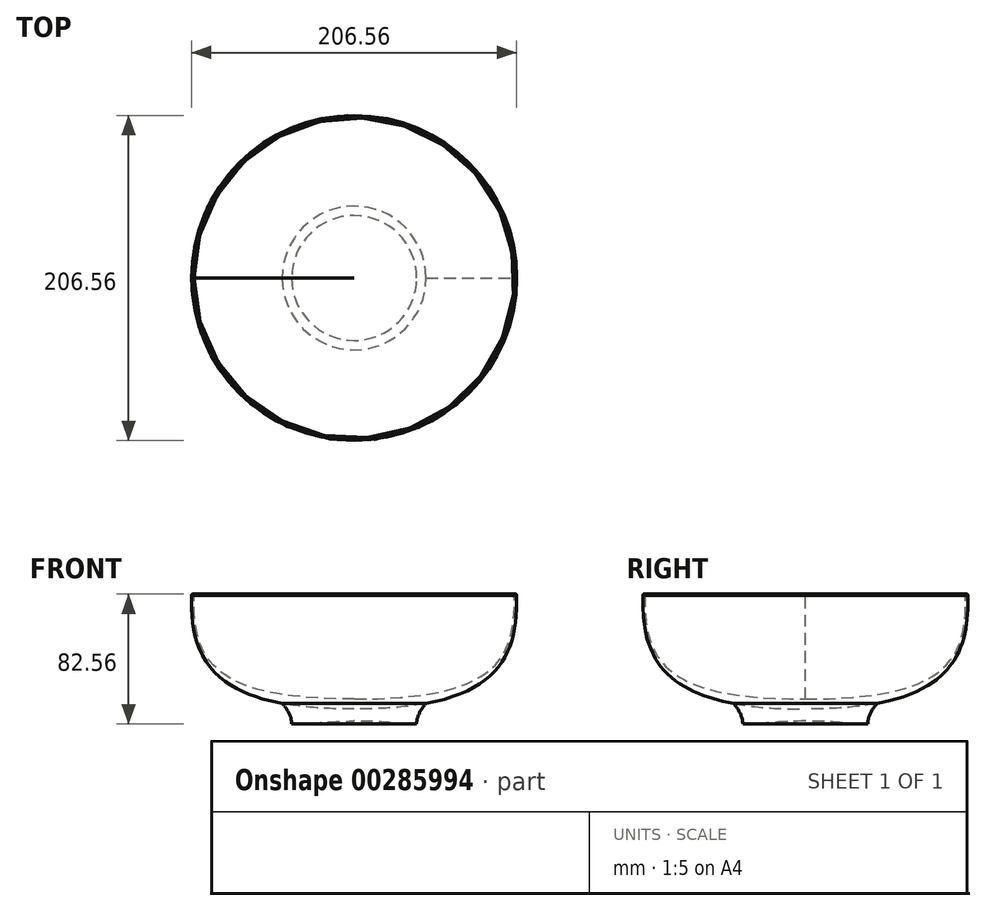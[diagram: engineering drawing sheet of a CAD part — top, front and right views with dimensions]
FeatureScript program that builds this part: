
annotation { "Feature Type Name" : "Feature", "Feature Type Description" : "" }
export const myFeature = defineFeature(function(context is Context, id is Id, definition is map)
    precondition{}
    {
        {
            var Q0;
            Q0=qCreatedBy(makeId("Front.planeOp"),FACE);
            var sketch = newSketch(context, id + "F0", { "sketchPlane" : qUnion([Q0])});
            skLineSegment(sketch, "E0", {"start": v(0, 113.79) * mm, "end": v(0, -78.4) * mm});
            skFitSpline(sketch, "E1", {"points": [v(0, 0) * mm, v(-103.19, 73.03) * mm], "startDerivative": vector(-262.4, 0) * mm, "endDerivative": vector(4.55, 131.95) * mm});
            skFitSpline(sketch, "E2", {"points": [v(-45.67, 3.6) * mm, v(-39.69, -9.53) * mm], "startDerivative": vector(9.2, -9.94) * mm, "endDerivative": vector(0.03, -14.95) * mm});
            skFitSpline(sketch, "E3.MirrorCS", {"points": [v(45.67, 3.6) * mm, v(39.69, -9.53) * mm], "startDerivative": vector(-9.2, -9.94) * mm, "endDerivative": vector(-0.03, -14.95) * mm});
            skFitSpline(sketch, "E4.MirrorCS", {"points": [v(0, 0) * mm, v(103.19, 73.03) * mm], "startDerivative": vector(262.4, 0) * mm, "endDerivative": vector(-4.55, 131.95) * mm});
            skFitSpline(sketch, "E5", {"points": [v(-39.69, -9.53) * mm, v(-35.15, -9.53) * mm, v(0, -7.62) * mm, v(35.15, -9.53) * mm, v(39.69, -9.53) * mm], "startDerivative": vector(100.22, 7.27) * mm, "endDerivative": vector(100.48, 0) * mm});
            skLineSegment(sketch, "E6", {"start": v(-103.19, 73.03) * mm, "end": v(103.19, 73.03) * mm});
            skFitSpline(sketch, "E7", {"points": [v(0, 6.35) * mm, v(-101.66, 73.03) * mm], "startDerivative": vector(-262.4, 0) * mm, "endDerivative": vector(4.55, 131.95) * mm});
            skFitSpline(sketch, "E8.MirrorCS", {"points": [v(0, 6.35) * mm, v(101.66, 73.03) * mm], "startDerivative": vector(262.4, 0) * mm, "endDerivative": vector(-4.55, 131.95) * mm});
            skSolve(sketch);
        }
        {
            var Q0;
            {var subQ4=sQuery(id+"F0.wireOp",EDGE,"E7");Q0=makeQuery(id+"F0.imprint","IMPRINT",FACE,{"disambiguationData":[TD([[makeQuery(id+"F0.imprint","IMPRINT",EDGE,{"derivedFrom":subQ4}),1.0]])]});}
            var Q1;
            Q1=sQuery(id+"F0.wireOp",EDGE,"E0");
            revolve(context, id + "F1", {"entities" : qUnion([Q0]), "axis" : qUnion([Q1]), "revolveType" : RevolveType.FULL});
        }
        {
            var Q0;
            Q0=makeQuery(id+"F1.opRevolve","SWEPT_EDGE",EDGE,{"disambiguationData":[OSD([sQuery(id+"F0.wireOp",EDGE,"E6"),sQuery(id+"F0.wireOp",EDGE,"E7")])]});
            var Q1;
            Q1=makeQuery(id+"F1.opRevolve","SWEPT_EDGE",EDGE,{"disambiguationData":[OSD([sQuery(id+"F0.wireOp",EDGE,"E1"),sQuery(id+"F0.wireOp",EDGE,"E6")])]});
            fillet(context, id + "F2", {"entities" : qUnion([Q0, Q1]), "radius" : 0.74 * mm, "tangentPropagation" : true, "allowEdgeOverflow" : false});
        }
        {
            var Q0;
            {var subQ5=sQuery(id+"F0.wireOp",EDGE,"E2");Q0=makeQuery(id+"F0.imprint","IMPRINT",FACE,{"disambiguationData":[TD([[makeQuery(id+"F0.imprint","IMPRINT",EDGE,{"derivedFrom":subQ5}),1.0]])]});}
            var Q1;
            Q1=sQuery(id+"F0.wireOp",EDGE,"E0");
            revolve(context, id + "F3", {"entities" : qUnion([Q0]), "axis" : qUnion([Q1]), "revolveType" : RevolveType.FULL});
        }
    });
